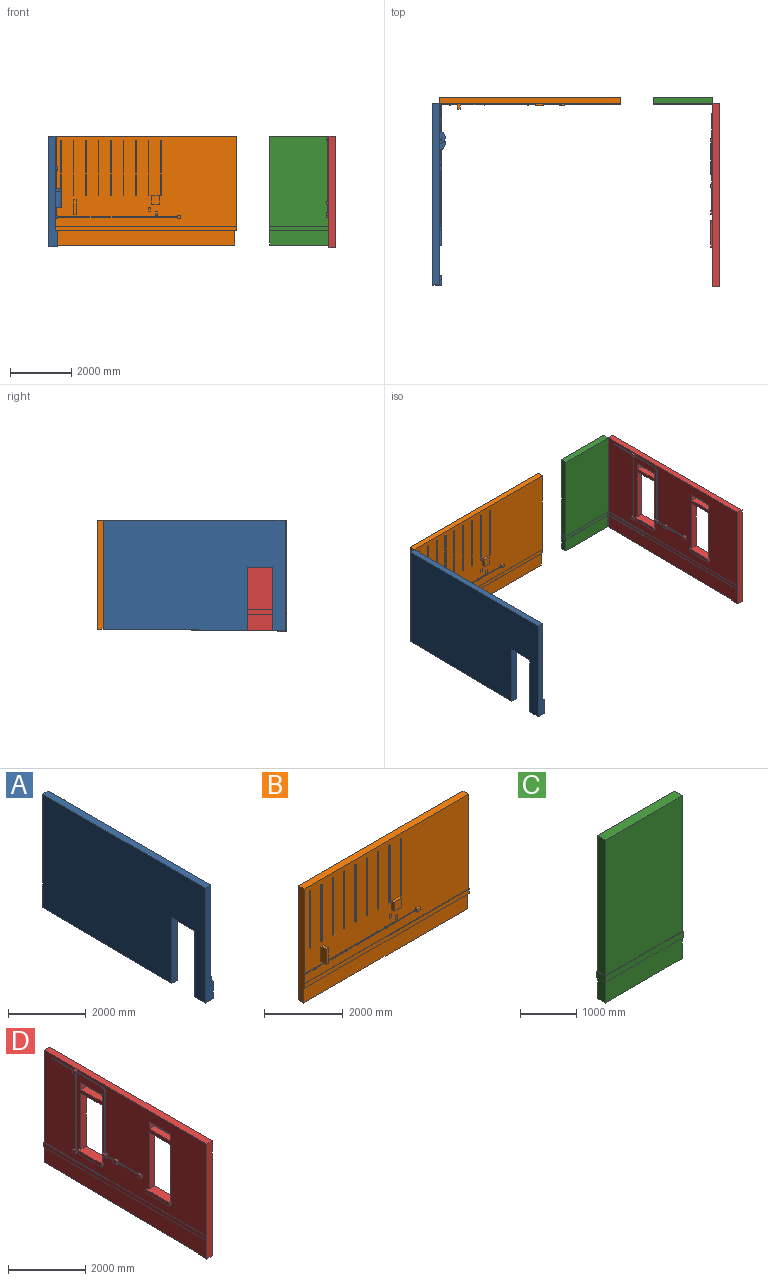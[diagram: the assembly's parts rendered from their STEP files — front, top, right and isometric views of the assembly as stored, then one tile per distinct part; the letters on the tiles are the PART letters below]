
ASSEMBLY  parts=4 mates=3
PART A: 127 faces, bbox 408x5915.6x3613.2 mm
  f0: plane 5915.61x2882.9mm, normal (1,0,0), area 14825475.2mm2, adj f9,f11,f12,f22,f24,f26,f27,f28
  f1: plane 3.18x0.03mm, normal (0,0,1), area 0mm2, adj f72,f77,f93
  f2: plane 3.18x0.03mm, normal (0,0,-1), area 0mm2, adj f72,f77,f93
  f3: plane 3.18x0.02mm, normal (0,0,1), area 0mm2, adj f78,f83,f91
  f4: plane 3.18x0.02mm, normal (0,0,-1), area 0mm2, adj f78,f83,f91
  f5: plane 484.19x17.15mm, normal (1,0,0), area 8301.4mm2, adj f47,f57,f58,f71
  f6: plane 484.19x17.15mm, normal (-1,0,0), area 8301.4mm2, adj f47,f57,f58,f71
  f7: plane 4702.76x292.1mm, normal (0,0.01,-1), area 1365699.4mm2, adj f8,f11,f14,f15,f19,f29
  f8: plane 5915.61x3613.15mm, normal (-1,0,0), area 19522929.3mm2, adj f7,f9,f10,f11,f12,f19,f20,f21
  f9: plane 3613.15x292.1mm, normal (0,-1,0), area 784111.3mm2, adj f0,f8,f10,f12,f17,f18,f24,f25
  f10: plane 396.88x292.1mm, normal (0,0.01,-1), area 107892.9mm2, adj f8,f9,f16,f18,f21,f29
  f11: plane 3556x292.1mm, normal (0,1,0), area 767417.8mm2, adj f0,f7,f8,f12,f13,f15,f22,f23
  f12: plane 5915.61x203.2mm, normal (0,0,1), area 1202051.1mm2, adj f0,f8,f9,f11
  f13: plane 4610.68x76.2mm, normal (0,0,1), area 351333.9mm2, adj f11,f14,f15,f23
  f14: plane 717.64x87.31mm, normal (0,-1,0), area 47659.3mm2, adj f7,f13,f15,f22,f23,f29
  f15: plane 4610.68x520.79mm, normal (1,0,0), area 2298524.1mm2, adj f7,f11,f13,f14
  f16: plane 727.31x87.31mm, normal (0,1,0), area 48502.9mm2, adj f10,f17,f18,f24,f25,f29
  f17: plane 304.8x76.2mm, normal (0,0,1), area 23225.8mm2, adj f9,f16,f18,f25
  f18: plane 533.4x304.8mm, normal (1,0,0), area 162131.6mm2, adj f9,f10,f16,f17
  f19: plane 2057.4x204.79mm, normal (0,-1,0), area 421329.8mm2, adj f7,f8,f20,f29
  f20: plane 815.98x204.79mm, normal (0,0,-1), area 167101.5mm2, adj f8,f19,f21,f29
  f21: plane 2065.28x204.79mm, normal (0,1,0), area 422944.2mm2, adj f8,f10,f20,f29
  f22: plane 4610.68x12.7mm, normal (0,0,1), area 58555.6mm2, adj f0,f11,f14,f23,f26
  f23: plane 4610.68x196.85mm, normal (1,0,0), area 907612.5mm2, adj f11,f13,f14,f22
  f24: plane 304.8x12.7mm, normal (0,0,1), area 3871mm2, adj f0,f9,f16,f25,f28
  f25: plane 304.8x196.85mm, normal (1,0,0), area 59999.9mm2, adj f9,f16,f17,f24
  f26: plane 1441.36x1.59mm, normal (0,1,0), area 2288.2mm2, adj f0,f22,f27,f29
  f27: plane 1000.13x1.59mm, normal (0,0,1), area 1587.7mm2, adj f0,f26,f28,f29
  f28: plane 1441.36x1.59mm, normal (0,-1,0), area 2288.2mm2, adj f0,f24,f27,f29
  f29: plane 2168.66x1000.13mm, normal (1,0,0), area 482098.4mm2, adj f7,f10,f14,f16,f19,f20,f21,f26
  f30: plane 104.78x76.2mm, normal (0,1,0), area 7657.2mm2, adj f0,f31,f33,f34,f59,f60,f61,f62
  f31: plane 104.78x76.2mm, normal (0,0,1), area 7983.9mm2, adj f0,f30,f32,f34
  f32: plane 104.78x76.2mm, normal (0,-1,0), area 7983.9mm2, adj f0,f31,f33,f34
  f33: plane 104.78x76.2mm, normal (0,0,-1), area 7983.9mm2, adj f0,f30,f32,f34
  f34: plane 104.78x104.78mm, normal (1,0,0), area 10977.8mm2, adj f30,f31,f32,f33
  f35: plane 104.78x76.2mm, normal (0,1,0), area 7657.2mm2, adj f0,f36,f38,f39,f63,f64,f65,f66
  f36: plane 104.78x76.2mm, normal (0,0,1), area 7983.9mm2, adj f0,f35,f37,f39
  f37: plane 104.78x76.2mm, normal (0,-1,0), area 7657.2mm2, adj f0,f36,f38,f39,f59,f60,f61,f62
  f38: plane 104.78x76.2mm, normal (0,0,-1), area 7983.9mm2, adj f0,f35,f37,f39
  f39: plane 104.78x104.78mm, normal (1,0,0), area 10977.8mm2, adj f35,f36,f37,f38
  f40: plane 104.78x76.2mm, normal (0,1,0), area 7657.2mm2, adj f0,f41,f43,f44,f67,f68,f69,f70
  f41: plane 104.78x76.2mm, normal (0,0,1), area 7983.9mm2, adj f0,f40,f42,f44
  f42: plane 104.78x76.2mm, normal (0,-1,0), area 7657.2mm2, adj f0,f41,f43,f44,f63,f64,f65,f66
  f43: plane 104.78x76.2mm, normal (0,0,-1), area 7983.9mm2, adj f0,f40,f42,f44
  f44: plane 104.78x104.78mm, normal (1,0,0), area 10977.8mm2, adj f40,f41,f42,f43
  f45: plane 104.78x76.2mm, normal (0,-1,0), area 7657.2mm2, adj f0,f46,f48,f49,f67,f68,f69,f70
  f46: plane 104.78x76.2mm, normal (0,0,-1), area 7983.9mm2, adj f0,f45,f47,f49
  f47: plane 104.78x76.2mm, normal (0,1,0), area 7657.2mm2, adj f0,f5,f6,f46,f48,f49,f57,f58
  f48: plane 104.78x76.2mm, normal (0,0,1), area 7657.2mm2, adj f0,f45,f47,f49,f52,f54,f55,f56
  f49: plane 104.78x104.78mm, normal (1,0,0), area 10977.8mm2, adj f45,f46,f47,f48
  f50: cylinder r=50.8mm len=101.6mm, axis (-1,0,0), area 24322mm2, adj f0,f51
  f51: plane 101.6x101.6mm, normal (1,0,0), area 8107.3mm2, adj f50
  f52: plane 2578.1x19.05mm, normal (0,1,0), area 49112.8mm2, adj f48,f53,f55,f56
  f53: plane 19.05x17.15mm, normal (0,0,1), area 326.6mm2, adj f52,f54,f55,f56
  f54: plane 2578.1x19.05mm, normal (0,-1,0), area 49112.8mm2, adj f48,f53,f55,f56
  f55: plane 2578.1x17.15mm, normal (1,0,0), area 44201.5mm2, adj f48,f52,f53,f54
  f56: plane 2578.1x17.15mm, normal (-1,0,0), area 44201.5mm2, adj f48,f52,f53,f54
  f57: plane 484.19x19.05mm, normal (0,0,-1), area 9223.8mm2, adj f5,f6,f47,f71
  f58: plane 484.19x19.05mm, normal (0,0,1), area 9223.8mm2, adj f5,f6,f47,f71
  f59: plane 1835.15x19.05mm, normal (0,0,-1), area 34959.6mm2, adj f30,f37,f61,f62
  f60: plane 1835.15x19.05mm, normal (0,0,1), area 34959.6mm2, adj f30,f37,f61,f62
  f61: plane 1835.15x17.15mm, normal (1,0,0), area 31463.6mm2, adj f30,f37,f59,f60
  f62: plane 1835.15x17.15mm, normal (-1,0,0), area 31463.6mm2, adj f30,f37,f59,f60
  f63: plane 104.78x19.05mm, normal (0,0,1), area 1996mm2, adj f35,f42,f65,f66
  f64: plane 104.78x19.05mm, normal (0,0,-1), area 1996mm2, adj f35,f42,f65,f66
  f65: plane 104.78x17.15mm, normal (1,0,0), area 1796.4mm2, adj f35,f42,f63,f64
  f66: plane 104.78x17.15mm, normal (-1,0,0), area 1796.4mm2, adj f35,f42,f63,f64
  f67: plane 1248.36x19.05mm, normal (0,0,1), area 23781.2mm2, adj f40,f45,f69,f70
  f68: plane 1248.36x19.05mm, normal (0,0,-1), area 23781.2mm2, adj f40,f45,f69,f70
  f69: plane 1248.36x17.15mm, normal (1,0,0), area 21403.1mm2, adj f40,f45,f67,f68
  f70: plane 1248.36x17.15mm, normal (-1,0,0), area 21403.1mm2, adj f40,f45,f67,f68
  f71: plane 19.05x17.15mm, normal (0,1,0), area 326.6mm2, adj f5,f6,f57,f58
  f72: plane 438.15x3.18mm, normal (0,-1,0), area 1391.1mm2, adj f1,f2,f77,f93
  f73: plane 390.53x3.18mm, normal (0,0,-1), area 1239.9mm2, adj f0,f74,f76,f77
  f74: plane 787.4x3.18mm, normal (0,1,0), area 2500mm2, adj f0,f73,f75,f77
  f75: plane 390.53x3.18mm, normal (0,0,1), area 1239.9mm2, adj f0,f74,f76,f77
  f76: plane 787.4x3.18mm, normal (0,-1,0), area 2500mm2, adj f0,f73,f75,f77
  f77: plane 787.4x390.53mm, normal (1,0,0), area 180021.8mm2, adj f1,f2,f72,f73,f74,f75,f76,f94
  f78: plane 520.7x3.18mm, normal (0,1,0), area 1653.2mm2, adj f3,f4,f83,f91
  f79: plane 388.94x3.18mm, normal (0,0,-1), area 1234.9mm2, adj f0,f80,f82,f83
  f80: plane 660.4x3.18mm, normal (0,1,0), area 2096.8mm2, adj f0,f79,f81,f83
  f81: plane 388.94x3.18mm, normal (0,0,1), area 1234.9mm2, adj f0,f80,f82,f83
  f82: plane 660.4x3.18mm, normal (0,-1,0), area 2096.8mm2, adj f0,f79,f81,f83
  f83: plane 660.4x388.94mm, normal (1,0,0), area 102879.4mm2, adj f3,f4,f78,f79,f80,f81,f82,f89
  f84: plane 79.38x3.18mm, normal (0,0,-1), area 252mm2, adj f0,f85,f87,f88
  f85: plane 123.83x3.18mm, normal (0,1,0), area 393.1mm2, adj f0,f84,f86,f88
  f86: plane 79.38x3.18mm, normal (0,0,1), area 252mm2, adj f0,f85,f87,f88
  f87: plane 123.83x3.18mm, normal (0,-1,0), area 393.1mm2, adj f0,f84,f86,f88
  f88: plane 123.83x79.38mm, normal (1,0,0), area 9828.6mm2, adj f84,f85,f86,f87
  f89: plane 409.43x201.61mm, normal (0,0,-1), area 64349.5mm2, adj f83,f91,f92
  f90: plane 309.59x201.61mm, normal (0,0,1), area 39854.1mm2, adj f83,f91,f92,f93,f95
  f91: cylinder r=204.79mm len=520.7mm, axis (0,0,-1), area 259211.6mm2, adj f3,f4,f78,f89,f90,f92,f93,f94
  f92: plane 520.7x113.74mm, normal (-1,0.03,0), area 22358.1mm2, adj f83,f89,f90,f91,f94,f95
  f93: cylinder r=200.03mm len=438.15mm, axis (0,0,1), area 198966.8mm2, adj f1,f2,f72,f90,f91,f94,f95,f96
  f94: plane 300.01x196.85mm, normal (0,0,-1), area 36874.5mm2, adj f77,f91,f92,f93,f95
  f95: plane 438.15x108.98mm, normal (-1,-0.03,0), area 12554.6mm2, adj f77,f90,f92,f93,f94,f96
  f96: plane 399.9x196.85mm, normal (0,0,1), area 61369.9mm2, adj f77,f93,f95
  f97: plane 25.4x22.23mm, normal (0,0,-1), area 564.5mm2, adj f0,f98,f100,f101
  f98: plane 1206.5x25.4mm, normal (0,1,0), area 30645.1mm2, adj f0,f97,f99,f101
  f99: plane 25.4x22.23mm, normal (0,0,1), area 564.5mm2, adj f0,f98,f100,f101
  f100: plane 1206.5x25.4mm, normal (0,-1,0), area 30645.1mm2, adj f0,f97,f99,f101
  f101: plane 1206.5x22.23mm, normal (1,0,0), area 26814.5mm2, adj f97,f98,f99,f100
  f102: plane 25.4x22.23mm, normal (0,0,1), area 564.5mm2, adj f0,f103,f105,f106
  f103: plane 1206.5x25.4mm, normal (0,-1,0), area 30645.1mm2, adj f0,f102,f104,f106
  f104: plane 25.4x22.23mm, normal (0,0,-1), area 564.5mm2, adj f0,f103,f105,f106
  f105: plane 1206.5x25.4mm, normal (0,1,0), area 30645.1mm2, adj f0,f102,f104,f106
  f106: plane 1206.5x22.23mm, normal (1,0,0), area 26814.5mm2, adj f102,f103,f104,f105
  f107: plane 25.4x22.23mm, normal (0,0,1), area 564.5mm2, adj f0,f108,f110,f111
  f108: plane 1206.5x25.4mm, normal (0,-1,0), area 30645.1mm2, adj f0,f107,f109,f111
  f109: plane 25.4x22.23mm, normal (0,0,-1), area 564.5mm2, adj f0,f108,f110,f111
  f110: plane 1206.5x25.4mm, normal (0,1,0), area 30645.1mm2, adj f0,f107,f109,f111
  f111: plane 1206.5x22.23mm, normal (1,0,0), area 26814.5mm2, adj f107,f108,f109,f110
  f112: plane 25.4x22.23mm, normal (0,0,1), area 564.5mm2, adj f0,f113,f115,f116
  f113: plane 1206.5x25.4mm, normal (0,-1,0), area 30645.1mm2, adj f0,f112,f114,f116
  f114: plane 25.4x22.23mm, normal (0,0,-1), area 564.5mm2, adj f0,f113,f115,f116
  f115: plane 1206.5x25.4mm, normal (0,1,0), area 30645.1mm2, adj f0,f112,f114,f116
  f116: plane 1206.5x22.23mm, normal (1,0,0), area 26814.5mm2, adj f112,f113,f114,f115
  f117: plane 25.4x22.23mm, normal (0,0,1), area 564.5mm2, adj f0,f118,f120,f121
  f118: plane 1206.5x25.4mm, normal (0,-1,0), area 30645.1mm2, adj f0,f117,f119,f121
  f119: plane 25.4x22.23mm, normal (0,0,-1), area 564.5mm2, adj f0,f118,f120,f121
  f120: plane 1206.5x25.4mm, normal (0,1,0), area 30645.1mm2, adj f0,f117,f119,f121
  f121: plane 1206.5x22.23mm, normal (1,0,0), area 26814.5mm2, adj f117,f118,f119,f120
  f122: plane 25.4x22.23mm, normal (0,0,1), area 564.5mm2, adj f0,f123,f125,f126
  f123: plane 1206.5x25.4mm, normal (0,-1,0), area 30645.1mm2, adj f0,f122,f124,f126
  f124: plane 25.4x22.23mm, normal (0,0,-1), area 564.5mm2, adj f0,f123,f125,f126
  f125: plane 1206.5x25.4mm, normal (0,1,0), area 30645.1mm2, adj f0,f122,f124,f126
  f126: plane 1206.5x22.23mm, normal (1,0,0), area 26814.5mm2, adj f122,f123,f124,f125
PART B: 123 faces, bbox 5916.6x393.7x3556 mm
  f0: plane 5903.91x2946.4mm, normal (0,-1,0), area 16890722.3mm2, adj f4,f6,f9,f10,f14,f15,f16,f17
  f1: plane 341.31x19.05mm, normal (0,0,1), area 6502mm2, adj f47,f71,f72,f77
  f2: plane 341.31x19.05mm, normal (0,0,-1), area 6502mm2, adj f47,f71,f72,f77
  f3: plane 5865.81x187.33mm, normal (0,0,-1), area 1098813.3mm2, adj f5,f6,f8,f12
  f4: plane 5903.91x203.2mm, normal (0,0,1), area 1199675mm2, adj f0,f5,f6,f9
  f5: plane 5916.61x3556mm, normal (0,1,0), area 20977861.3mm2, adj f3,f4,f6,f7,f9,f10,f11,f12
  f6: plane 3556x215.9mm, normal (-1,0,0), area 716712.3mm2, adj f0,f3,f4,f5,f7,f8,f10,f13
  f7: plane 5916.61x215.9mm, normal (0,0,-1), area 178583.3mm2, adj f5,f6,f8,f11,f12,f13
  f8: plane 5865.81x476.25mm, normal (0,-1,0), area 2793593.2mm2, adj f3,f6,f7,f12
  f9: plane 2946.4x203.2mm, normal (1,0,0), area 598708.5mm2, adj f0,f4,f5,f10
  f10: plane 5916.61x215.9mm, normal (0,0,1), area 77721.6mm2, adj f0,f5,f6,f9,f11,f13
  f11: plane 215.9x133.35mm, normal (1,0,0), area 28790.3mm2, adj f5,f7,f10,f13
  f12: plane 476.25x187.33mm, normal (1,0,0), area 89213.5mm2, adj f3,f5,f7,f8
  f13: plane 5916.61x133.35mm, normal (0,-1,0), area 788980.3mm2, adj f6,f7,f10,f11
  f14: plane 476.25x190.5mm, normal (-1,0,0), area 90725.6mm2, adj f0,f15,f17,f18
  f15: plane 190.5x95.25mm, normal (0,0,-1), area 18145.1mm2, adj f0,f14,f16,f18
  f16: plane 476.25x190.5mm, normal (1,0,0), area 90725.6mm2, adj f0,f15,f17,f18
  f17: plane 190.5x95.25mm, normal (0,0,1), area 18145.1mm2, adj f0,f14,f16,f18
  f18: plane 476.25x95.25mm, normal (0,-1,0), area 45362.8mm2, adj f14,f15,f16,f17
  f19: plane 254x76.2mm, normal (0,0,-1), area 19354.8mm2, adj f0,f20,f22,f23
  f20: plane 279.4x76.2mm, normal (1,0,0), area 21290.3mm2, adj f0,f19,f21,f23
  f21: plane 254x76.2mm, normal (0,0,1), area 19354.8mm2, adj f0,f20,f22,f23
  f22: plane 279.4x76.2mm, normal (-1,0,0), area 21290.3mm2, adj f0,f19,f21,f23
  f23: plane 279.4x254mm, normal (0,-1,0), area 70967.6mm2, adj f19,f20,f21,f22
  f24: plane 104.78x76.2mm, normal (-1,0,0), area 7681.4mm2, adj f0,f25,f27,f28,f73,f74,f75,f76
  f25: plane 104.78x76.2mm, normal (0,0,-1), area 7983.9mm2, adj f0,f24,f26,f28
  f26: plane 104.78x76.2mm, normal (1,0,0), area 7983.9mm2, adj f0,f25,f27,f28
  f27: plane 104.78x76.2mm, normal (0,0,1), area 7983.9mm2, adj f0,f24,f26,f28
  f28: plane 104.78x104.78mm, normal (0,-1,0), area 10977.8mm2, adj f24,f25,f26,f27
  f29: plane 79.38x3.18mm, normal (0,0,-1), area 252mm2, adj f0,f30,f32,f33
  f30: plane 127x3.18mm, normal (1,0,0), area 403.2mm2, adj f0,f29,f31,f33
  f31: plane 79.38x3.18mm, normal (0,0,1), area 252mm2, adj f0,f30,f32,f33
  f32: plane 127x3.18mm, normal (-1,0,0), area 403.2mm2, adj f0,f29,f31,f33
  f33: plane 127x79.38mm, normal (0,-1,0), area 10080.6mm2, adj f29,f30,f31,f32
  f34: plane 79.38x3.18mm, normal (0,0,-1), area 252mm2, adj f0,f35,f37,f38
  f35: plane 127x3.18mm, normal (1,0,0), area 403.2mm2, adj f0,f34,f36,f38
  f36: plane 79.38x3.18mm, normal (0,0,1), area 252mm2, adj f0,f35,f37,f38
  f37: plane 127x3.18mm, normal (-1,0,0), area 403.2mm2, adj f0,f34,f36,f38
  f38: plane 127x79.38mm, normal (0,-1,0), area 10080.6mm2, adj f34,f35,f36,f37
  f39: plane 50.8x19.05mm, normal (-1,0,0), area 665.3mm2, adj f0,f40,f42,f43,f67,f68,f69,f70
  f40: plane 50.8x19.05mm, normal (0,0,-1), area 967.7mm2, adj f0,f39,f41,f43
  f41: plane 50.8x19.05mm, normal (1,0,0), area 665.3mm2, adj f0,f40,f42,f43,f73,f74,f75,f76
  f42: plane 50.8x19.05mm, normal (0,0,1), area 967.7mm2, adj f0,f39,f41,f43
  f43: plane 19.05x19.05mm, normal (0,-1,0), area 362.9mm2, adj f39,f40,f41,f42
  f44: plane 50.8x19.05mm, normal (0,0,-1), area 967.7mm2, adj f0,f45,f47,f48
  f45: plane 50.8x19.05mm, normal (1,0,0), area 665.3mm2, adj f0,f44,f46,f48,f63,f64,f65,f66
  f46: plane 50.8x19.05mm, normal (0,0,1), area 967.7mm2, adj f0,f45,f47,f48
  f47: plane 50.8x19.05mm, normal (-1,0,0), area 665.3mm2, adj f0,f1,f2,f44,f46,f48,f71,f72
  f48: plane 19.05x19.05mm, normal (0,-1,0), area 362.9mm2, adj f44,f45,f46,f47
  f49: plane 50.8x19.05mm, normal (1,0,0), area 665.3mm2, adj f0,f50,f52,f53,f67,f68,f69,f70
  f50: plane 50.8x19.05mm, normal (0,0,1), area 967.7mm2, adj f0,f49,f51,f53
  f51: plane 50.8x19.05mm, normal (-1,0,0), area 665.3mm2, adj f0,f50,f52,f53,f59,f60,f61,f62
  f52: plane 50.8x19.05mm, normal (0,0,-1), area 967.7mm2, adj f0,f49,f51,f53
  f53: plane 19.05x19.05mm, normal (0,-1,0), area 362.9mm2, adj f49,f50,f51,f52
  f54: plane 50.8x19.05mm, normal (0,0,1), area 967.7mm2, adj f0,f55,f57,f58
  f55: plane 50.8x19.05mm, normal (-1,0,0), area 665.3mm2, adj f0,f54,f56,f58,f63,f64,f65,f66
  f56: plane 50.8x19.05mm, normal (0,0,-1), area 967.7mm2, adj f0,f55,f57,f58
  f57: plane 50.8x19.05mm, normal (1,0,0), area 665.3mm2, adj f0,f54,f56,f58,f59,f60,f61,f62
  f58: plane 19.05x19.05mm, normal (0,-1,0), area 362.9mm2, adj f54,f55,f56,f57
  f59: plane 1397x15.88mm, normal (0,1,0), area 22177.4mm2, adj f51,f57,f61,f62
  f60: plane 1397x15.88mm, normal (0,-1,0), area 22177.4mm2, adj f51,f57,f61,f62
  f61: plane 1397x19.05mm, normal (0,0,1), area 26612.8mm2, adj f51,f57,f59,f60
  f62: plane 1397x19.05mm, normal (0,0,-1), area 26612.8mm2, adj f51,f57,f59,f60
  f63: plane 1098.55x15.88mm, normal (0,1,0), area 17439.5mm2, adj f45,f55,f65,f66
  f64: plane 1098.55x15.88mm, normal (0,-1,0), area 17439.5mm2, adj f45,f55,f65,f66
  f65: plane 1098.55x19.05mm, normal (0,0,1), area 20927.4mm2, adj f45,f55,f63,f64
  f66: plane 1098.55x19.05mm, normal (0,0,-1), area 20927.4mm2, adj f45,f55,f63,f64
  f67: plane 1035.05x15.88mm, normal (0,1,0), area 16431.4mm2, adj f39,f49,f69,f70
  f68: plane 1035.05x15.88mm, normal (0,-1,0), area 16431.4mm2, adj f39,f49,f69,f70
  f69: plane 1035.05x19.05mm, normal (0,0,1), area 19717.7mm2, adj f39,f49,f67,f68
  f70: plane 1035.05x19.05mm, normal (0,0,-1), area 19717.7mm2, adj f39,f49,f67,f68
  f71: plane 341.31x15.88mm, normal (0,1,0), area 5418.3mm2, adj f1,f2,f47,f77
  f72: plane 341.31x15.88mm, normal (0,-1,0), area 5418.3mm2, adj f1,f2,f47,f77
  f73: plane 23.81x19.05mm, normal (0,0,-1), area 453.6mm2, adj f24,f41,f75,f76
  f74: plane 23.81x19.05mm, normal (0,0,1), area 453.6mm2, adj f24,f41,f75,f76
  f75: plane 23.81x15.88mm, normal (0,-1,0), area 378mm2, adj f24,f41,f73,f74
  f76: plane 23.81x15.88mm, normal (0,1,0), area 378mm2, adj f24,f41,f73,f74
  f77: plane 19.05x15.88mm, normal (-1,0,0), area 302.4mm2, adj f1,f2,f71,f72
  f78: plane 1778x25.4mm, normal (-1,0,0), area 45161.2mm2, adj f0,f79,f81,f82
  f79: plane 25.4x22.23mm, normal (0,0,-1), area 564.5mm2, adj f0,f78,f80,f82
  f80: plane 1778x25.4mm, normal (1,0,0), area 45161.2mm2, adj f0,f79,f81,f82
  f81: plane 25.4x22.23mm, normal (0,0,1), area 564.5mm2, adj f0,f78,f80,f82
  f82: plane 1778x22.23mm, normal (0,-1,0), area 39516mm2, adj f78,f79,f80,f81
  f83: plane 1778x25.4mm, normal (1,0,0), area 45161.2mm2, adj f0,f84,f86,f87
  f84: plane 25.4x22.23mm, normal (0,0,1), area 564.5mm2, adj f0,f83,f85,f87
  f85: plane 1778x25.4mm, normal (-1,0,0), area 45161.2mm2, adj f0,f84,f86,f87
  f86: plane 25.4x22.23mm, normal (0,0,-1), area 564.5mm2, adj f0,f83,f85,f87
  f87: plane 1778x22.23mm, normal (0,-1,0), area 39516.1mm2, adj f83,f84,f85,f86
  f88: plane 1778x25.4mm, normal (1,0,0), area 45161.2mm2, adj f0,f89,f91,f92
  f89: plane 25.4x22.23mm, normal (0,0,1), area 564.5mm2, adj f0,f88,f90,f92
  f90: plane 1778x25.4mm, normal (-1,0,0), area 45161.2mm2, adj f0,f89,f91,f92
  f91: plane 25.4x22.23mm, normal (0,0,-1), area 564.5mm2, adj f0,f88,f90,f92
  f92: plane 1778x22.23mm, normal (0,-1,0), area 39516mm2, adj f88,f89,f90,f91
  f93: plane 1778x25.4mm, normal (1,0,0), area 45161.2mm2, adj f0,f94,f96,f97
  f94: plane 25.4x22.23mm, normal (0,0,1), area 564.5mm2, adj f0,f93,f95,f97
  f95: plane 1778x25.4mm, normal (-1,0,0), area 45161.2mm2, adj f0,f94,f96,f97
  f96: plane 25.4x22.23mm, normal (0,0,-1), area 564.5mm2, adj f0,f93,f95,f97
  f97: plane 1778x22.23mm, normal (0,-1,0), area 39516mm2, adj f93,f94,f95,f96
  f98: plane 1778x25.4mm, normal (1,0,0), area 45161.2mm2, adj f0,f99,f101,f102
  f99: plane 25.4x22.23mm, normal (0,0,1), area 564.5mm2, adj f0,f98,f100,f102
  f100: plane 1778x25.4mm, normal (-1,0,0), area 45161.2mm2, adj f0,f99,f101,f102
  f101: plane 25.4x22.23mm, normal (0,0,-1), area 564.5mm2, adj f0,f98,f100,f102
  f102: plane 1778x22.23mm, normal (0,-1,0), area 39516.1mm2, adj f98,f99,f100,f101
  f103: plane 1778x25.4mm, normal (1,0,0), area 45161.2mm2, adj f0,f104,f106,f107
  f104: plane 25.4x22.23mm, normal (0,0,1), area 564.5mm2, adj f0,f103,f105,f107
  f105: plane 1778x25.4mm, normal (-1,0,0), area 45161.2mm2, adj f0,f104,f106,f107
  f106: plane 25.4x22.23mm, normal (0,0,-1), area 564.5mm2, adj f0,f103,f105,f107
  f107: plane 1778x22.23mm, normal (0,-1,0), area 39516mm2, adj f103,f104,f105,f106
  f108: plane 1778x25.4mm, normal (1,0,0), area 45161.2mm2, adj f0,f109,f111,f112
  f109: plane 25.4x22.23mm, normal (0,0,1), area 564.5mm2, adj f0,f108,f110,f112
  f110: plane 1778x25.4mm, normal (-1,0,0), area 45161.2mm2, adj f0,f109,f111,f112
  f111: plane 25.4x22.23mm, normal (0,0,-1), area 564.5mm2, adj f0,f108,f110,f112
  f112: plane 1778x22.23mm, normal (0,-1,0), area 39516.1mm2, adj f108,f109,f110,f111
  f113: plane 1778x25.4mm, normal (1,0,0), area 45161.2mm2, adj f0,f114,f116,f117
  f114: plane 25.4x22.23mm, normal (0,0,1), area 564.5mm2, adj f0,f113,f115,f117
  f115: plane 1778x25.4mm, normal (-1,0,0), area 45161.2mm2, adj f0,f114,f116,f117
  f116: plane 25.4x22.23mm, normal (0,0,-1), area 564.5mm2, adj f0,f113,f115,f117
  f117: plane 1778x22.23mm, normal (0,-1,0), area 39516.1mm2, adj f113,f114,f115,f116
  f118: plane 1778x25.4mm, normal (1,0,0), area 45161.2mm2, adj f0,f119,f121,f122
  f119: plane 25.4x22.23mm, normal (0,0,1), area 564.5mm2, adj f0,f118,f120,f122
  f120: plane 1778x25.4mm, normal (-1,0,0), area 45161.2mm2, adj f0,f119,f121,f122
  f121: plane 25.4x22.23mm, normal (0,0,-1), area 564.5mm2, adj f0,f118,f120,f122
  f122: plane 1778x22.23mm, normal (0,-1,0), area 39516.1mm2, adj f118,f119,f120,f121
PART C: 12 faces, bbox 1955.8x215.9x3556 mm
  f0: plane 2946.4x1943.1mm, normal (0,-1,0), area 5725149.8mm2, adj f1,f4,f7,f8
  f1: plane 3556x215.9mm, normal (1,0,0), area 716712.3mm2, adj f0,f2,f3,f4,f5,f6,f8,f11
  f2: plane 1930.4x476.25mm, normal (0,-1,0), area 919353mm2, adj f1,f5,f6,f10
  f3: plane 3556x1955.8mm, normal (0,1,0), area 6905308.8mm2, adj f1,f4,f5,f6,f7,f8,f9,f10
  f4: plane 1943.1x203.2mm, normal (0,0,1), area 394837.9mm2, adj f0,f1,f3,f7
  f5: plane 1930.4x187.33mm, normal (0,0,-1), area 361612.2mm2, adj f1,f2,f3,f10
  f6: plane 1955.8x215.9mm, normal (0,0,-1), area 60645mm2, adj f1,f2,f3,f9,f10,f11
  f7: plane 2946.4x203.2mm, normal (-1,0,0), area 598708.5mm2, adj f0,f3,f4,f8
  f8: plane 1955.8x215.9mm, normal (0,0,1), area 27419.3mm2, adj f0,f1,f3,f7,f9,f11
  f9: plane 215.9x133.35mm, normal (-1,0,0), area 28790.3mm2, adj f3,f6,f8,f11
  f10: plane 476.25x187.33mm, normal (-1,0,0), area 89213.5mm2, adj f2,f3,f5,f6
  f11: plane 1955.8x133.35mm, normal (0,-1,0), area 260805.9mm2, adj f1,f6,f8,f9
PART D: 86 faces, bbox 279.4x5969x3651.3 mm
  f0: plane 5969x584.2mm, normal (-1,0,0), area 3117277mm2, adj f3,f4,f5,f6,f7,f83
  f1: plane 5969x2933.7mm, normal (-1,0,0), area 14129210.7mm2, adj f3,f7,f8,f9,f10,f11,f12,f13
  f2: plane 5969x3651.25mm, normal (1,0,0), area 18278310.2mm2, adj f3,f4,f5,f6,f7,f8,f9,f10
  f3: plane 3651.25x215.9mm, normal (0,-1,0), area 743627.5mm2, adj f0,f1,f2,f4,f8,f83,f84,f85
  f4: plane 285.75x203.2mm, normal (0,0,-1), area 58064.4mm2, adj f0,f2,f3,f5
  f5: plane 203.2x34.93mm, normal (0,1,0), area 7096.8mm2, adj f0,f2,f4,f6
  f6: plane 5683.25x203.2mm, normal (0,0.01,-1), area 1154901.4mm2, adj f0,f2,f5,f7
  f7: plane 3556.03x215.9mm, normal (0,1,0), area 724279.6mm2, adj f0,f1,f2,f6,f8,f83,f84,f85
  f8: plane 5969x203.2mm, normal (0,0,1), area 1212900.8mm2, adj f1,f2,f3,f7
  f9: plane 222.25x203.2mm, normal (0,1,0), area 45161.2mm2, adj f1,f2,f10,f12
  f10: plane 777.88x203.2mm, normal (0,0,1), area 158064.2mm2, adj f1,f2,f9,f11
  f11: plane 222.25x203.2mm, normal (0,-1,0), area 45161.2mm2, adj f1,f2,f10,f12
  f12: plane 777.88x203.2mm, normal (0,0,-1), area 158064.2mm2, adj f1,f2,f9,f11
  f13: plane 863.6x279.4mm, normal (0,0,1), area 223870.5mm2, adj f1,f2,f14,f16,f25,f26,f28
  f14: plane 1793.88x203.2mm, normal (0,-1,0), area 364515.4mm2, adj f1,f2,f13,f15
  f15: plane 777.88x203.2mm, normal (0,0,-1), area 158064.2mm2, adj f1,f2,f14,f16
  f16: plane 1793.88x203.2mm, normal (0,1,0), area 364515.4mm2, adj f1,f2,f13,f15
  f17: plane 863.6x279.4mm, normal (0,0,1), area 224838.3mm2, adj f1,f2,f18,f20,f29,f30,f32
  f18: plane 1793.88x203.2mm, normal (0,-1,0), area 364515.4mm2, adj f1,f2,f17,f19
  f19: plane 782.64x203.2mm, normal (0,0,-1), area 159031.9mm2, adj f1,f2,f18,f20
  f20: plane 1793.88x203.2mm, normal (0,1,0), area 364515.4mm2, adj f1,f2,f17,f19
  f21: plane 782.64x203.2mm, normal (0,0,1), area 159031.9mm2, adj f1,f2,f22,f24
  f22: plane 222.25x203.2mm, normal (0,-1,0), area 45161.2mm2, adj f1,f2,f21,f23
  f23: plane 782.64x203.2mm, normal (0,0,-1), area 159031.9mm2, adj f1,f2,f22,f24
  f24: plane 222.25x203.2mm, normal (0,1,0), area 45161.2mm2, adj f1,f2,f21,f23
  f25: plane 104.78x76.2mm, normal (0,1,0), area 7983.9mm2, adj f1,f13,f27,f28
  f26: plane 104.78x76.2mm, normal (0,-1,0), area 7983.9mm2, adj f1,f13,f27,f28
  f27: plane 863.6x76.2mm, normal (0,0,-1), area 65806.3mm2, adj f1,f25,f26,f28
  f28: plane 863.6x104.78mm, normal (-1,0,0), area 90483.7mm2, adj f13,f25,f26,f27
  f29: plane 104.78x76.2mm, normal (0,1,0), area 7983.9mm2, adj f1,f17,f31,f32
  f30: plane 104.78x76.2mm, normal (0,-1,0), area 7983.9mm2, adj f1,f17,f31,f32
  f31: plane 863.6x76.2mm, normal (0,0,-1), area 65806.3mm2, adj f1,f29,f30,f32
  f32: plane 863.6x104.78mm, normal (-1,0,0), area 90483.7mm2, adj f17,f29,f30,f31
  f33: plane 104.78x76.2mm, normal (0,1,0), area 7560.5mm2, adj f1,f34,f36,f37,f58,f59,f60,f61
  f34: plane 104.78x76.2mm, normal (0,0,1), area 7983.9mm2, adj f1,f33,f35,f37
  f35: plane 104.78x76.2mm, normal (0,-1,0), area 7983.9mm2, adj f1,f34,f36,f37
  f36: plane 104.78x76.2mm, normal (0,0,-1), area 7983.9mm2, adj f1,f33,f35,f37
  f37: plane 104.78x104.78mm, normal (-1,0,0), area 10977.8mm2, adj f33,f34,f35,f36
  f38: plane 104.78x76.2mm, normal (0,1,0), area 7560.5mm2, adj f1,f39,f41,f42,f62,f63,f64,f65
  f39: plane 104.78x76.2mm, normal (0,0,1), area 7983.9mm2, adj f1,f38,f40,f42
  f40: plane 104.78x76.2mm, normal (0,-1,0), area 7560.5mm2, adj f1,f39,f41,f42,f58,f59,f60,f61
  f41: plane 104.78x76.2mm, normal (0,0,-1), area 7983.9mm2, adj f1,f38,f40,f42
  f42: plane 104.78x104.78mm, normal (-1,0,0), area 10977.8mm2, adj f38,f39,f40,f41
  f43: plane 104.78x76.2mm, normal (0,-1,0), area 7560.5mm2, adj f1,f44,f46,f47,f62,f63,f64,f65
  f44: plane 104.78x76.2mm, normal (0,0,-1), area 7983.9mm2, adj f1,f43,f45,f47
  f45: plane 104.78x76.2mm, normal (0,1,0), area 7983.9mm2, adj f1,f44,f46,f47
  f46: plane 104.78x76.2mm, normal (0,0,1), area 7681.4mm2, adj f1,f43,f45,f47,f69,f70,f72,f73
  f47: plane 104.78x104.78mm, normal (-1,0,0), area 10977.8mm2, adj f43,f44,f45,f46
  f48: plane 104.78x76.2mm, normal (0,0,-1), area 7983.9mm2, adj f1,f49,f51,f52
  f49: plane 104.78x76.2mm, normal (0,1,0), area 7983.9mm2, adj f1,f48,f50,f52
  f50: plane 104.78x76.2mm, normal (0,0,1), area 7681.4mm2, adj f1,f49,f51,f52,f74,f75,f76,f77
  f51: plane 104.78x76.2mm, normal (0,-1,0), area 7983.9mm2, adj f1,f48,f50,f52
  f52: plane 104.78x104.78mm, normal (-1,0,0), area 10977.8mm2, adj f48,f49,f50,f51
  f53: plane 104.78x76.2mm, normal (0,1,0), area 7681.4mm2, adj f1,f54,f56,f57,f78,f79,f81,f82
  f54: plane 104.78x76.2mm, normal (0,0,1), area 7983.9mm2, adj f1,f53,f55,f57
  f55: plane 104.78x76.2mm, normal (0,-1,0), area 7681.4mm2, adj f1,f54,f56,f57,f66,f67,f72,f73
  f56: plane 104.78x76.2mm, normal (0,0,-1), area 7681.4mm2, adj f1,f53,f55,f57,f74,f75,f76,f77
  f57: plane 104.78x104.78mm, normal (-1,0,0), area 10977.8mm2, adj f53,f54,f55,f56
  f58: plane 765.18x19.05mm, normal (0,0,-1), area 14576.6mm2, adj f33,f40,f60,f61
  f59: plane 765.18x19.05mm, normal (0,0,1), area 14576.6mm2, adj f33,f40,f60,f61
  f60: plane 765.18x22.23mm, normal (-1,0,0), area 17006mm2, adj f33,f40,f58,f59
  f61: plane 765.18x22.23mm, normal (1,0,0), area 17006mm2, adj f33,f40,f58,f59
  f62: plane 314.33x19.05mm, normal (0,0,1), area 5987.9mm2, adj f38,f43,f64,f65
  f63: plane 314.33x19.05mm, normal (0,0,-1), area 5987.9mm2, adj f38,f43,f64,f65
  f64: plane 314.33x22.23mm, normal (-1,0,0), area 6985.9mm2, adj f38,f43,f62,f63
  f65: plane 314.33x22.23mm, normal (1,0,0), area 6985.9mm2, adj f38,f43,f62,f63
  f66: plane 925.51x19.05mm, normal (0,0,-1), area 17631mm2, adj f55,f71,f72,f73
  f67: plane 925.51x19.05mm, normal (0,0,1), area 17631mm2, adj f55,f68,f72,f73
  f68: cylinder r=101.6mm len=101.6mm, axis (1,0,0), area 3040.2mm2, adj f67,f69,f72,f73
  f69: plane 1962.15x19.05mm, normal (0,-1,0), area 37379mm2, adj f46,f68,f72,f73
  f70: plane 1962.15x19.05mm, normal (0,1,0), area 37379mm2, adj f46,f71,f72,f73
  f71: cylinder r=85.72mm len=85.73mm, axis (1,0,0), area 2565.2mm2, adj f66,f70,f72,f73
  f72: plane 2063.75x1027.11mm, normal (-1,0,0), area 48177.2mm2, adj f46,f55,f66,f67,f68,f69,f70,f71
  f73: plane 2063.75x1027.11mm, normal (1,0,0), area 48177.2mm2, adj f46,f55,f66,f67,f68,f69,f70,f71
  f74: plane 2409.83x19.05mm, normal (0,-1,0), area 45907.2mm2, adj f50,f56,f76,f77
  f75: plane 2409.83x19.05mm, normal (0,1,0), area 45907.2mm2, adj f50,f56,f76,f77
  f76: plane 2409.83x15.88mm, normal (-1,0,0), area 38256mm2, adj f50,f56,f74,f75
  f77: plane 2409.83x15.88mm, normal (1,0,0), area 38256mm2, adj f50,f56,f74,f75
  f78: plane 812.8x19.05mm, normal (0,0,1), area 15483.8mm2, adj f53,f80,f81,f82
  f79: plane 812.8x19.05mm, normal (0,0,-1), area 15483.8mm2, adj f53,f80,f81,f82
  f80: plane 19.05x15.88mm, normal (0,1,0), area 302.4mm2, adj f78,f79,f81,f82
  f81: plane 812.8x15.88mm, normal (-1,0,0), area 12903.2mm2, adj f53,f78,f79,f80
  f82: plane 812.8x15.88mm, normal (1,0,0), area 12903.2mm2, adj f53,f78,f79,f80
  f83: plane 5969x12.7mm, normal (0,0,-1), area 75806.3mm2, adj f0,f3,f7,f85
  f84: plane 5969x12.7mm, normal (0,0,1), area 75806.3mm2, adj f1,f3,f7,f85
  f85: plane 5969x133.35mm, normal (-1,0,0), area 795966.1mm2, adj f3,f7,f83,f84
PLACE A t=(0,-15.88,0)mm
PLACE B t=(0,-15.87,0)mm
PLACE C t=(0,-15.87,0)mm
PLACE D t=(8932.86,-15.88,0)mm
MATE fastened D.f8 <-> C.f4  axis (0,0,1) through (8932.86,-15.87,3556)mm
MATE fastened B.f0 <-> C.f0  axis (0,-1,0) through (5903.91,-15.87,3556)mm
MATE fastened A.f12 <-> B.f4  axis (0,0,1) through (0,-15.87,3556)mm
